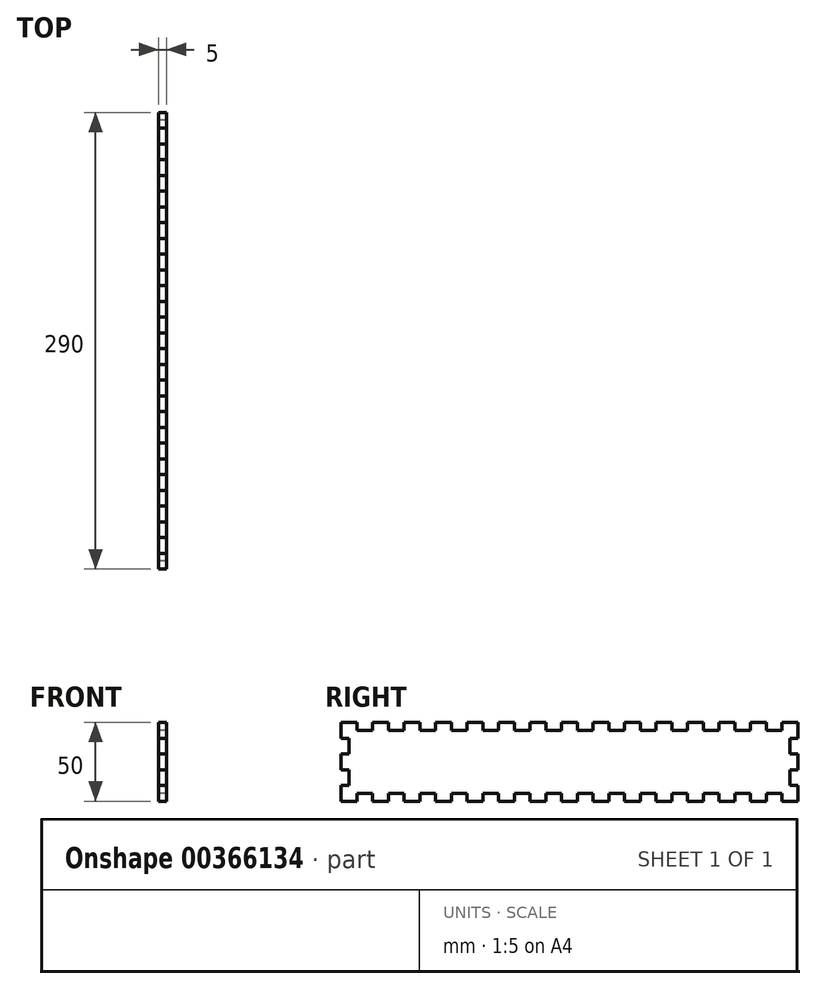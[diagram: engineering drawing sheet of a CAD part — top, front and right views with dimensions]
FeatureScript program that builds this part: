
annotation { "Feature Type Name" : "Feature", "Feature Type Description" : "" }
export const myFeature = defineFeature(function(context is Context, id is Id, definition is map)
    precondition{}
    {
        {
            var Q0;
            Q0=qCreatedBy(makeId("Right.planeOp"),FACE);
            var sketch = newSketch(context, id + "F0", { "sketchPlane" : qUnion([Q0])});
            skPoint(sketch, "E0.middle", {"position": v(0, 0) * mm});
            skLineSegment(sketch, "E1", {"start": v(-145, 25) * mm, "end": v(-135, 25) * mm});
            skLineSegment(sketch, "E2", {"start": v(-135, 25) * mm, "end": v(-135, 20) * mm});
            skLineSegment(sketch, "E3", {"start": v(-135, 20) * mm, "end": v(-125, 20) * mm});
            skLineSegment(sketch, "E4", {"start": v(-125, 20) * mm, "end": v(-125, 25) * mm});
            skLineSegment(sketch, "E5.1.0.0", {"start": v(-125, 25) * mm, "end": v(-115, 25) * mm});
            skLineSegment(sketch, "E5.1.0.1", {"start": v(-115, 25) * mm, "end": v(-115, 20) * mm});
            skLineSegment(sketch, "E5.1.0.2", {"start": v(-115, 20) * mm, "end": v(-105, 20) * mm});
            skLineSegment(sketch, "E5.1.0.3", {"start": v(-105, 20) * mm, "end": v(-105, 25) * mm});
            skLineSegment(sketch, "E5.2.0.0", {"start": v(-105, 25) * mm, "end": v(-95, 25) * mm});
            skLineSegment(sketch, "E5.2.0.1", {"start": v(-95, 25) * mm, "end": v(-95, 20) * mm});
            skLineSegment(sketch, "E5.2.0.2", {"start": v(-95, 20) * mm, "end": v(-85, 20) * mm});
            skLineSegment(sketch, "E5.2.0.3", {"start": v(-85, 20) * mm, "end": v(-85, 25) * mm});
            skLineSegment(sketch, "E5.3.0.0", {"start": v(-85, 25) * mm, "end": v(-75, 25) * mm});
            skLineSegment(sketch, "E5.3.0.1", {"start": v(-75, 25) * mm, "end": v(-75, 20) * mm});
            skLineSegment(sketch, "E5.3.0.2", {"start": v(-75, 20) * mm, "end": v(-65, 20) * mm});
            skLineSegment(sketch, "E5.3.0.3", {"start": v(-65, 20) * mm, "end": v(-65, 25) * mm});
            skLineSegment(sketch, "E5.4.0.0", {"start": v(-65, 25) * mm, "end": v(-55, 25) * mm});
            skLineSegment(sketch, "E5.4.0.1", {"start": v(-55, 25) * mm, "end": v(-55, 20) * mm});
            skLineSegment(sketch, "E5.4.0.2", {"start": v(-55, 20) * mm, "end": v(-45, 20) * mm});
            skLineSegment(sketch, "E5.4.0.3", {"start": v(-45, 20) * mm, "end": v(-45, 25) * mm});
            skLineSegment(sketch, "E5.5.0.0", {"start": v(-45, 25) * mm, "end": v(-35, 25) * mm});
            skLineSegment(sketch, "E5.5.0.1", {"start": v(-35, 25) * mm, "end": v(-35, 20) * mm});
            skLineSegment(sketch, "E5.5.0.2", {"start": v(-35, 20) * mm, "end": v(-25, 20) * mm});
            skLineSegment(sketch, "E5.5.0.3", {"start": v(-25, 20) * mm, "end": v(-25, 25) * mm});
            skLineSegment(sketch, "E5.6.0.0", {"start": v(-25, 25) * mm, "end": v(-15, 25) * mm});
            skLineSegment(sketch, "E5.6.0.1", {"start": v(-15, 25) * mm, "end": v(-15, 20) * mm});
            skLineSegment(sketch, "E5.6.0.2", {"start": v(-15, 20) * mm, "end": v(-5, 20) * mm});
            skLineSegment(sketch, "E5.6.0.3", {"start": v(-5, 20) * mm, "end": v(-5, 25) * mm});
            skLineSegment(sketch, "E5.7.0.0", {"start": v(-5, 25) * mm, "end": v(5, 25) * mm});
            skLineSegment(sketch, "E5.7.0.1", {"start": v(5, 25) * mm, "end": v(5, 20) * mm});
            skLineSegment(sketch, "E5.7.0.2", {"start": v(5, 20) * mm, "end": v(15, 20) * mm});
            skLineSegment(sketch, "E5.7.0.3", {"start": v(15, 20) * mm, "end": v(15, 25) * mm});
            skLineSegment(sketch, "E5.8.0.0", {"start": v(15, 25) * mm, "end": v(25, 25) * mm});
            skLineSegment(sketch, "E5.8.0.1", {"start": v(25, 25) * mm, "end": v(25, 20) * mm});
            skLineSegment(sketch, "E5.8.0.2", {"start": v(25, 20) * mm, "end": v(35, 20) * mm});
            skLineSegment(sketch, "E5.8.0.3", {"start": v(35, 20) * mm, "end": v(35, 25) * mm});
            skLineSegment(sketch, "E5.9.0.0", {"start": v(35, 25) * mm, "end": v(45, 25) * mm});
            skLineSegment(sketch, "E5.9.0.1", {"start": v(45, 25) * mm, "end": v(45, 20) * mm});
            skLineSegment(sketch, "E5.9.0.2", {"start": v(45, 20) * mm, "end": v(55, 20) * mm});
            skLineSegment(sketch, "E5.9.0.3", {"start": v(55, 20) * mm, "end": v(55, 25) * mm});
            skLineSegment(sketch, "E5.10.0.0", {"start": v(55, 25) * mm, "end": v(65, 25) * mm});
            skLineSegment(sketch, "E5.10.0.1", {"start": v(65, 25) * mm, "end": v(65, 20) * mm});
            skLineSegment(sketch, "E5.10.0.2", {"start": v(65, 20) * mm, "end": v(75, 20) * mm});
            skLineSegment(sketch, "E5.10.0.3", {"start": v(75, 20) * mm, "end": v(75, 25) * mm});
            skLineSegment(sketch, "E5.11.0.0", {"start": v(75, 25) * mm, "end": v(85, 25) * mm});
            skLineSegment(sketch, "E5.11.0.1", {"start": v(85, 25) * mm, "end": v(85, 20) * mm});
            skLineSegment(sketch, "E5.11.0.2", {"start": v(85, 20) * mm, "end": v(95, 20) * mm});
            skLineSegment(sketch, "E5.11.0.3", {"start": v(95, 20) * mm, "end": v(95, 25) * mm});
            skLineSegment(sketch, "E5.12.0.0", {"start": v(95, 25) * mm, "end": v(105, 25) * mm});
            skLineSegment(sketch, "E5.12.0.1", {"start": v(105, 25) * mm, "end": v(105, 20) * mm});
            skLineSegment(sketch, "E5.12.0.2", {"start": v(105, 20) * mm, "end": v(115, 20) * mm});
            skLineSegment(sketch, "E5.12.0.3", {"start": v(115, 20) * mm, "end": v(115, 25) * mm});
            skLineSegment(sketch, "E5.13.0.0", {"start": v(115, 25) * mm, "end": v(125, 25) * mm});
            skLineSegment(sketch, "E5.13.0.1", {"start": v(125, 25) * mm, "end": v(125, 20) * mm});
            skLineSegment(sketch, "E5.13.0.2", {"start": v(125, 20) * mm, "end": v(135, 20) * mm});
            skLineSegment(sketch, "E5.13.0.3", {"start": v(135, 20) * mm, "end": v(135, 25) * mm});
            skLineSegment(sketch, "E6", {"start": v(135, 25) * mm, "end": v(145, 25) * mm});
            skLineSegment(sketch, "E7", {"start": v(-135, -25) * mm, "end": v(-135, -20) * mm});
            skLineSegment(sketch, "E8", {"start": v(-135, -20) * mm, "end": v(-125, -20) * mm});
            skLineSegment(sketch, "E9", {"start": v(-125, -20) * mm, "end": v(-125, -25) * mm});
            skLineSegment(sketch, "E10", {"start": v(-145, -25) * mm, "end": v(-135, -25) * mm});
            skLineSegment(sketch, "E11.1.0.0", {"start": v(-125, -25) * mm, "end": v(-115, -25) * mm});
            skLineSegment(sketch, "E11.1.0.1", {"start": v(-115, -25) * mm, "end": v(-115, -20) * mm});
            skLineSegment(sketch, "E11.1.0.2", {"start": v(-115, -20) * mm, "end": v(-105, -20) * mm});
            skLineSegment(sketch, "E11.1.0.3", {"start": v(-105, -20) * mm, "end": v(-105, -25) * mm});
            skLineSegment(sketch, "E11.2.0.0", {"start": v(-105, -25) * mm, "end": v(-95, -25) * mm});
            skLineSegment(sketch, "E11.2.0.1", {"start": v(-95, -25) * mm, "end": v(-95, -20) * mm});
            skLineSegment(sketch, "E11.2.0.2", {"start": v(-95, -20) * mm, "end": v(-85, -20) * mm});
            skLineSegment(sketch, "E11.2.0.3", {"start": v(-85, -20) * mm, "end": v(-85, -25) * mm});
            skLineSegment(sketch, "E11.3.0.0", {"start": v(-85, -25) * mm, "end": v(-75, -25) * mm});
            skLineSegment(sketch, "E11.3.0.1", {"start": v(-75, -25) * mm, "end": v(-75, -20) * mm});
            skLineSegment(sketch, "E11.3.0.2", {"start": v(-75, -20) * mm, "end": v(-65, -20) * mm});
            skLineSegment(sketch, "E11.3.0.3", {"start": v(-65, -20) * mm, "end": v(-65, -25) * mm});
            skLineSegment(sketch, "E11.4.0.0", {"start": v(-65, -25) * mm, "end": v(-55, -25) * mm});
            skLineSegment(sketch, "E11.4.0.1", {"start": v(-55, -25) * mm, "end": v(-55, -20) * mm});
            skLineSegment(sketch, "E11.4.0.2", {"start": v(-55, -20) * mm, "end": v(-45, -20) * mm});
            skLineSegment(sketch, "E11.4.0.3", {"start": v(-45, -20) * mm, "end": v(-45, -25) * mm});
            skLineSegment(sketch, "E11.5.0.0", {"start": v(-45, -25) * mm, "end": v(-35, -25) * mm});
            skLineSegment(sketch, "E11.5.0.1", {"start": v(-35, -25) * mm, "end": v(-35, -20) * mm});
            skLineSegment(sketch, "E11.5.0.2", {"start": v(-35, -20) * mm, "end": v(-25, -20) * mm});
            skLineSegment(sketch, "E11.5.0.3", {"start": v(-25, -20) * mm, "end": v(-25, -25) * mm});
            skLineSegment(sketch, "E11.6.0.0", {"start": v(-25, -25) * mm, "end": v(-15, -25) * mm});
            skLineSegment(sketch, "E11.6.0.1", {"start": v(-15, -25) * mm, "end": v(-15, -20) * mm});
            skLineSegment(sketch, "E11.6.0.2", {"start": v(-15, -20) * mm, "end": v(-5, -20) * mm});
            skLineSegment(sketch, "E11.6.0.3", {"start": v(-5, -20) * mm, "end": v(-5, -25) * mm});
            skLineSegment(sketch, "E11.7.0.0", {"start": v(-5, -25) * mm, "end": v(5, -25) * mm});
            skLineSegment(sketch, "E11.7.0.1", {"start": v(5, -25) * mm, "end": v(5, -20) * mm});
            skLineSegment(sketch, "E11.7.0.2", {"start": v(5, -20) * mm, "end": v(15, -20) * mm});
            skLineSegment(sketch, "E11.7.0.3", {"start": v(15, -20) * mm, "end": v(15, -25) * mm});
            skLineSegment(sketch, "E11.8.0.0", {"start": v(15, -25) * mm, "end": v(25, -25) * mm});
            skLineSegment(sketch, "E11.8.0.1", {"start": v(25, -25) * mm, "end": v(25, -20) * mm});
            skLineSegment(sketch, "E11.8.0.2", {"start": v(25, -20) * mm, "end": v(35, -20) * mm});
            skLineSegment(sketch, "E11.8.0.3", {"start": v(35, -20) * mm, "end": v(35, -25) * mm});
            skLineSegment(sketch, "E11.9.0.0", {"start": v(35, -25) * mm, "end": v(45, -25) * mm});
            skLineSegment(sketch, "E11.9.0.1", {"start": v(45, -25) * mm, "end": v(45, -20) * mm});
            skLineSegment(sketch, "E11.9.0.2", {"start": v(45, -20) * mm, "end": v(55, -20) * mm});
            skLineSegment(sketch, "E11.9.0.3", {"start": v(55, -20) * mm, "end": v(55, -25) * mm});
            skLineSegment(sketch, "E11.10.0.0", {"start": v(55, -25) * mm, "end": v(65, -25) * mm});
            skLineSegment(sketch, "E11.10.0.1", {"start": v(65, -25) * mm, "end": v(65, -20) * mm});
            skLineSegment(sketch, "E11.10.0.2", {"start": v(65, -20) * mm, "end": v(75, -20) * mm});
            skLineSegment(sketch, "E11.10.0.3", {"start": v(75, -20) * mm, "end": v(75, -25) * mm});
            skLineSegment(sketch, "E11.11.0.0", {"start": v(75, -25) * mm, "end": v(85, -25) * mm});
            skLineSegment(sketch, "E11.11.0.1", {"start": v(85, -25) * mm, "end": v(85, -20) * mm});
            skLineSegment(sketch, "E11.11.0.2", {"start": v(85, -20) * mm, "end": v(95, -20) * mm});
            skLineSegment(sketch, "E11.11.0.3", {"start": v(95, -20) * mm, "end": v(95, -25) * mm});
            skLineSegment(sketch, "E11.12.0.0", {"start": v(95, -25) * mm, "end": v(105, -25) * mm});
            skLineSegment(sketch, "E11.12.0.1", {"start": v(105, -25) * mm, "end": v(105, -20) * mm});
            skLineSegment(sketch, "E11.12.0.2", {"start": v(105, -20) * mm, "end": v(115, -20) * mm});
            skLineSegment(sketch, "E11.12.0.3", {"start": v(115, -20) * mm, "end": v(115, -25) * mm});
            skLineSegment(sketch, "E11.13.0.0", {"start": v(115, -25) * mm, "end": v(125, -25) * mm});
            skLineSegment(sketch, "E11.13.0.1", {"start": v(125, -25) * mm, "end": v(125, -20) * mm});
            skLineSegment(sketch, "E11.13.0.2", {"start": v(125, -20) * mm, "end": v(135, -20) * mm});
            skLineSegment(sketch, "E11.13.0.3", {"start": v(135, -20) * mm, "end": v(135, -25) * mm});
            skLineSegment(sketch, "E12", {"start": v(135, -25) * mm, "end": v(145, -25) * mm});
            skLineSegment(sketch, "E13", {"start": v(145, -25) * mm, "end": v(145, -15) * mm});
            skLineSegment(sketch, "E14", {"start": v(145, -15) * mm, "end": v(140, -15) * mm});
            skLineSegment(sketch, "E15", {"start": v(140, -15) * mm, "end": v(140, -5) * mm});
            skLineSegment(sketch, "E16", {"start": v(140, -5) * mm, "end": v(145, -5) * mm});
            skLineSegment(sketch, "E17.1.0.0", {"start": v(145, -5) * mm, "end": v(145, 5) * mm});
            skLineSegment(sketch, "E17.1.0.1", {"start": v(145, 5) * mm, "end": v(140, 5) * mm});
            skLineSegment(sketch, "E17.1.0.2", {"start": v(140, 5) * mm, "end": v(140, 15) * mm});
            skLineSegment(sketch, "E17.1.0.3", {"start": v(140, 15) * mm, "end": v(145, 15) * mm});
            skLineSegment(sketch, "E18", {"start": v(145, 15) * mm, "end": v(145, 25) * mm});
            skLineSegment(sketch, "E19", {"start": v(-145, 25) * mm, "end": v(-145, 15) * mm});
            skLineSegment(sketch, "E20", {"start": v(-145, 15) * mm, "end": v(-140, 15) * mm});
            skLineSegment(sketch, "E21", {"start": v(-140, 15) * mm, "end": v(-140, 5) * mm});
            skLineSegment(sketch, "E22", {"start": v(-140, 5) * mm, "end": v(-145, 5) * mm});
            skLineSegment(sketch, "E23.1.0.0", {"start": v(-145, 5) * mm, "end": v(-145, -5) * mm});
            skLineSegment(sketch, "E23.1.0.1", {"start": v(-145, -5) * mm, "end": v(-140, -5) * mm});
            skLineSegment(sketch, "E23.1.0.2", {"start": v(-140, -5) * mm, "end": v(-140, -15) * mm});
            skLineSegment(sketch, "E23.1.0.3", {"start": v(-140, -15) * mm, "end": v(-145, -15) * mm});
            skLineSegment(sketch, "E24", {"start": v(-145, -15) * mm, "end": v(-145, -25) * mm});
            skSolve(sketch);
        }
        {
            var Q0;
            Q0 = qSketchRegion(id + "F0", true);
            extrude(context, id + "F1", {"entities" : qUnion([Q0]), "endBound" : BoundingType.SYMMETRIC, "depth" : 5 * mm});
        }
    });
